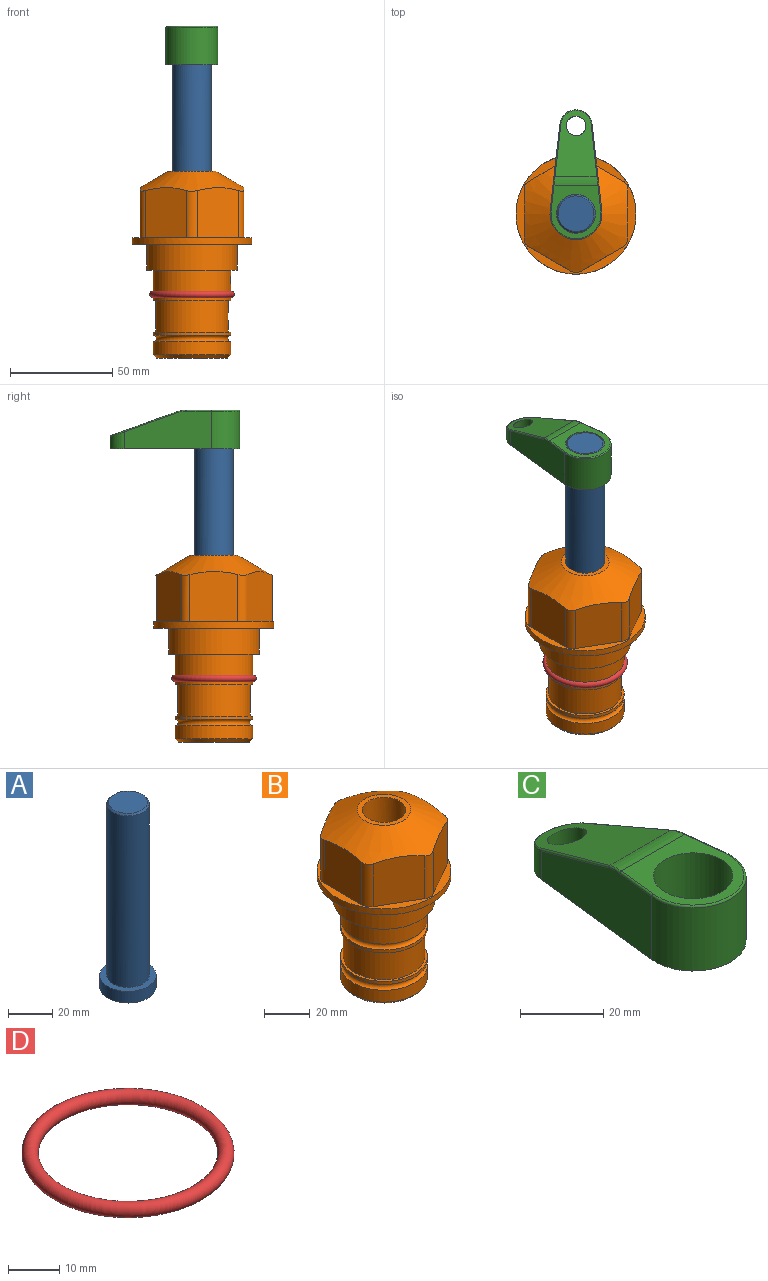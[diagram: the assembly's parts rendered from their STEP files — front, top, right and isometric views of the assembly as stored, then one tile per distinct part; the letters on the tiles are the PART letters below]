
ASSEMBLY  parts=4 mates=3
PART A: 6 faces, bbox 25.4x25.4x101.6 mm
  f0: plane 17.46x17.46mm, normal (0,0,1), area 239.5mm2, adj f5
  f1: plane 25.4x25.4mm, normal (0,0,-1), area 506.7mm2, adj f2
  f2: cylinder r=12.7mm len=25.4mm, axis (0,0,1), area 506.7mm2, adj f1,f3
  f3: plane 25.4x25.4mm, normal (0,0,1), area 221.7mm2, adj f2,f4
  f4: cylinder r=9.53mm len=94.46mm, axis (0,0,1), area 5653mm2, adj f3,f5
  f5: cone r=8.73mm half-angle=45deg, axis (0,0,-1), area 64.4mm2, adj f0,f4
PART B: 36 faces, bbox 58.7x58.7x91.2 mm
  f0: cylinder r=17.78mm len=35.56mm, axis (0,0,1), area 1670.8mm2, adj f23,f24,f31
  f1: cylinder r=19.05mm len=38.1mm, axis (0,0,1), area 1191.9mm2, adj f26,f27,f30
  f2: plane 58.66x58.66mm, normal (0,0,-1), area 1150.6mm2, adj f3,f28
  f3: cylinder r=29.33mm len=58.66mm, axis (0,0,-1), area 585.1mm2, adj f2,f4
  f4: plane 58.66x58.66mm, normal (0,0,1), area 475.9mm2, adj f3,f5,f6,f7,f8,f9,f10,f11
  f5: plane 24.5x20.32mm, normal (-0.5,0.87,0), area 562.8mm2, adj f4,f15,f16,f17
  f6: plane 24.5x20.32mm, normal (0.5,0.87,0), area 562.8mm2, adj f4,f14,f15,f17
  f7: plane 24.5x23.48mm, normal (1,0,0), area 562.8mm2, adj f4,f13,f14,f17
  f8: plane 24.5x20.32mm, normal (0.5,-0.87,0), area 562.8mm2, adj f4,f12,f13,f17
  f9: plane 24.5x20.32mm, normal (-0.5,-0.87,0), area 562.8mm2, adj f4,f11,f12,f17
  f10: plane 24.5x23.48mm, normal (-1,0,0), area 562.8mm2, adj f4,f11,f16,f17
  f11: cylinder r=5.08mm len=23.01mm, axis (0,0,-1), area 121.2mm2, adj f4,f9,f10,f17
  f12: cylinder r=5.08mm len=23.01mm, axis (0,0,-1), area 121.2mm2, adj f4,f8,f9,f17
  f13: cylinder r=5.08mm len=23.01mm, axis (0,0,-1), area 121.2mm2, adj f4,f7,f8,f17
  f14: cylinder r=5.08mm len=23.01mm, axis (0,0,-1), area 121.2mm2, adj f4,f6,f7,f17
  f15: cylinder r=5.08mm len=23.01mm, axis (0,0,-1), area 121.2mm2, adj f4,f5,f6,f17
  f16: cylinder r=5.08mm len=23.01mm, axis (0,0,-1), area 121.2mm2, adj f4,f5,f10,f17
  f17: cone r=11.73mm half-angle=60deg, axis (0,0,-1), area 2071.8mm2, adj f5,f6,f7,f8,f9,f10,f11,f12
  f18: plane 23.46x23.46mm, normal (0,0,1), area 147.4mm2, adj f17,f35
  f19: plane 34.93x34.93mm, normal (0,0,-1), area 958mm2, adj f29
  f20: cylinder r=19.05mm len=38.1mm, axis (0,0,1), area 760.1mm2, adj f21,f29
  f21: torus R=19.05mm, axis (0,0,1), area 565.3mm2, adj f20,f22
  f22: cylinder r=19.05mm len=38.1mm, axis (0,0,1), area 190mm2, adj f21,f23
  f23: plane 38.1x38.1mm, normal (0,0,1), area 146.9mm2, adj f0,f22
  f24: plane 38.1x38.1mm, normal (0,0,-1), area 146.9mm2, adj f0,f25
  f25: cylinder r=19.05mm len=38.1mm, axis (0,0,1), area 190mm2, adj f24,f26
  f26: torus R=19.05mm, axis (0,0,1), area 565.3mm2, adj f1,f25
  f27: plane 44.45x44.45mm, normal (0,0,-1), area 411.7mm2, adj f1,f28
  f28: cylinder r=22.23mm len=44.45mm, axis (0,0,1), area 1773.5mm2, adj f2,f27
  f29: cone r=19.05mm half-angle=45deg, axis (0,0,1), area 257.5mm2, adj f19,f20
  f30: cylinder r=3.17mm len=6.75mm, axis (-1,0,0), area 128mm2, adj f1,f33
  f31: cylinder r=3.17mm len=6.35mm, axis (-1,0,0), area 102.5mm2, adj f0,f33
  f32: plane 25.4x25.4mm, normal (0,0,1), area 506.7mm2, adj f33
  f33: cylinder r=12.7mm len=66.42mm, axis (0,0,-1), area 5236.2mm2, adj f30,f31,f32,f34
  f34: cone r=9.53mm half-angle=30deg, axis (0,0,-1), area 443.4mm2, adj f33,f35
  f35: cylinder r=9.53mm len=19.05mm, axis (0,0,-1), area 849mm2, adj f18,f34
PART C: 44 faces, bbox 27.5x64.5x19.1 mm
  f0: plane 2.3x0.95mm, normal (0,0,-1), area 1mm2, adj f25,f30,f34
  f1: plane 63.5x25.4mm, normal (0,0,-1), area 561.7mm2, adj f2,f3,f4,f5,f6,f7,f19,f20
  f2: cylinder r=12.7mm len=25.4mm, axis (0,0,-1), area 792.2mm2, adj f1,f3,f5,f13
  f3: plane 42.33x18.54mm, normal (0.99,0.11,0), area 647mm2, adj f1,f2,f4,f11,f12,f14
  f4: cylinder r=7.94mm len=15.78mm, axis (0,0,-1), area 158.6mm2, adj f1,f3,f5,f16
  f5: plane 42.33x18.54mm, normal (-0.99,0.11,0), area 647mm2, adj f1,f2,f4,f15,f17,f18
  f6: cylinder r=9.53mm len=19.05mm, axis (0,0,-1), area 1140.1mm2, adj f1,f8
  f7: cylinder r=4.76mm len=10.98mm, axis (0,0,-1), area 276.1mm2, adj f1,f9
  f8: plane 25.83x24.38mm, normal (0,0,1), area 262.2mm2, adj f6,f10,f11,f13,f15
  f9: plane 32.49x20.55mm, normal (0,0.34,0.94), area 489.9mm2, adj f7,f10,f14,f16,f18
  f10: cylinder r=12.7mm len=21.49mm, axis (-1,0,0), area 93.2mm2, adj f8,f9,f12,f17
  f11: cylinder r=0.51mm len=12.34mm, axis (0.11,-0.99,0), area 9.9mm2, adj f3,f8,f12,f13
  f12: bspline ~7.62x1.64mm, area 3.5mm2, adj f3,f10,f11,f14
  f13: torus R=12.19mm, axis (0,0,1), area 33.6mm2, adj f2,f8,f11,f15
  f14: cylinder r=0.51mm len=26.01mm, axis (0.1,-0.93,0.34), area 21.6mm2, adj f3,f9,f12,f16
  f15: cylinder r=0.51mm len=12.34mm, axis (0.11,0.99,0), area 9.9mm2, adj f5,f8,f13,f17
  f16: bspline ~15.78x7.05mm, area 15.7mm2, adj f4,f9,f14,f18
  f17: bspline ~7.62x1.64mm, area 3.5mm2, adj f5,f10,f15,f18
  f18: cylinder r=0.51mm len=26.01mm, axis (0.1,0.93,-0.34), area 21.6mm2, adj f5,f9,f16,f17
  f19: plane 21.6x14.29mm, normal (-0.99,-0.11,0), area 242.6mm2, adj f1,f26,f28,f34,f36,f38
  f20: plane 21.6x14.29mm, normal (0.99,-0.11,0), area 242.6mm2, adj f1,f27,f29,f37,f39,f41
  f21: cylinder r=12.7mm len=14.29mm, axis (0,0,-1), area 173.2mm2, adj f1,f26,f27,f30,f31,f33
  f22: cylinder r=7.94mm len=7.63mm, axis (0,0,-1), area 53.8mm2, adj f1,f28,f29,f42
  f23: plane 2.3x0.95mm, normal (0,0,-1), area 1mm2, adj f25,f33,f37
  f24: plane 17.94x12.32mm, normal (0,-0.34,-0.94), area 191.2mm2, adj f25,f38,f41,f42
  f25: cylinder r=9.53mm len=12.93mm, axis (-1,0,0), area 37.5mm2, adj f0,f23,f24,f31,f36,f39
  f26: cylinder r=1.59mm len=14.29mm, axis (0,0,-1), area 49mm2, adj f1,f19,f21,f32
  f27: cylinder r=1.59mm len=14.29mm, axis (0,0,-1), area 49mm2, adj f1,f20,f21,f35
  f28: cylinder r=1.59mm len=7.28mm, axis (0,0,-1), area 22.1mm2, adj f1,f19,f22,f40
  f29: cylinder r=1.59mm len=7.28mm, axis (0,0,-1), area 22.1mm2, adj f1,f20,f22,f43
  f30: torus R=14.29mm, axis (0,0,1), area 5.8mm2, adj f0,f21,f31,f32
  f31: bspline ~11.06x2.73mm, area 20.8mm2, adj f21,f25,f30,f33
  f32: sphere r=1.59mm, area 5.4mm2, adj f26,f30,f34
  f33: torus R=14.29mm, axis (0,0,1), area 5.8mm2, adj f21,f23,f31,f35
  f34: cylinder r=1.59mm len=1.68mm, axis (-0.11,0.99,0), area 2.4mm2, adj f0,f19,f32,f36
  f35: sphere r=1.59mm, area 5.4mm2, adj f27,f33,f37
  f36: bspline ~5.82x2.33mm, area 7.7mm2, adj f19,f25,f34,f38
  f37: cylinder r=1.59mm len=1.68mm, axis (0.11,0.99,0), area 2.4mm2, adj f20,f23,f35,f39
  f38: cylinder r=1.59mm len=18.33mm, axis (0.1,-0.93,0.34), area 46.7mm2, adj f19,f24,f36,f40
  f39: bspline ~5.82x2.33mm, area 7.7mm2, adj f20,f25,f37,f41
  f40: sphere r=1.59mm, area 3.6mm2, adj f28,f38,f42
  f41: cylinder r=1.59mm len=18.33mm, axis (0.1,0.93,-0.34), area 46.7mm2, adj f20,f24,f39,f43
  f42: bspline ~8.31x1.84mm, area 15.3mm2, adj f22,f24,f40,f43
  f43: sphere r=1.59mm, area 3.6mm2, adj f29,f41,f42
PART D: 1 faces, bbox 44.7x44.7x3.2 mm
  f0: torus R=19.05mm, axis (0,0,1), area 1193.9mm2
PLACE A t=(0.15,-13.26,32.97)mm
PLACE B t=(0.15,-13.26,0)mm
PLACE C t=(0.15,-13.26,87.58)mm
PLACE D t=(0.15,-13.26,0)mm
MATE cylindrical A.f2 <-> B.f0  axis (0,0,1) through (0.15,-13.26,58.61)mm
MATE fastened C.f2 <-> A.f2  axis (0,0,1) through (0.15,-13.26,106.63)mm
MATE cylindrical C.f2 <-> A.f2  axis (0,0,-1) through (0.15,-13.26,106.63)mm
